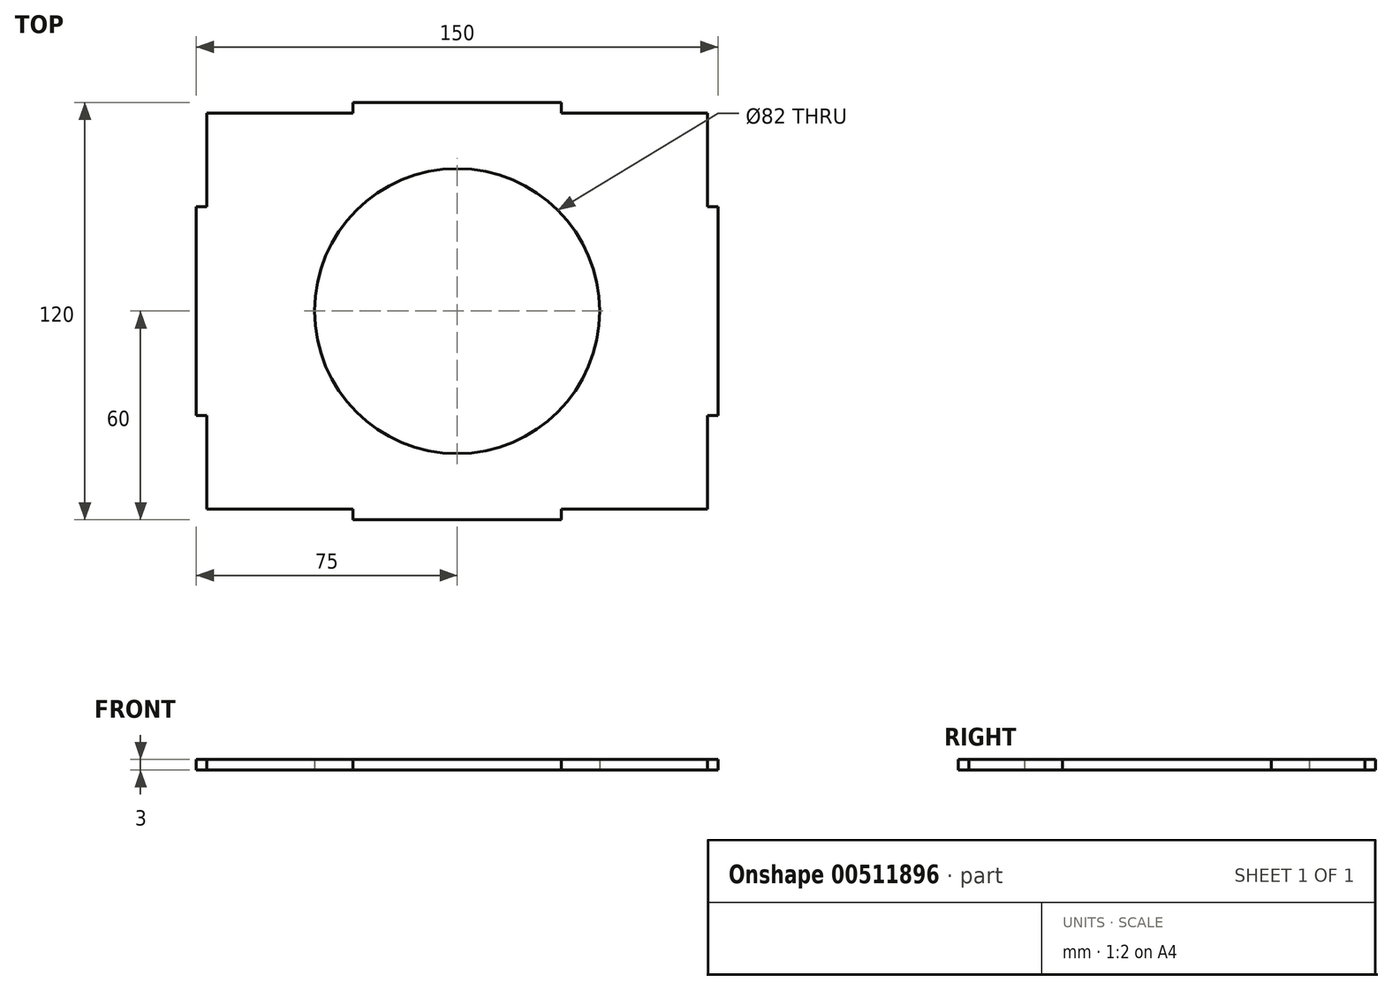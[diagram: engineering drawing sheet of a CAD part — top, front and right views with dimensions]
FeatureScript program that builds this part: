
annotation { "Feature Type Name" : "Feature", "Feature Type Description" : "" }
export const myFeature = defineFeature(function(context is Context, id is Id, definition is map)
    precondition{}
    {
        {
            var Q0;
            Q0=qCreatedBy(makeId("Top.planeOp"),FACE);
            var sketch = newSketch(context, id + "F0", { "sketchPlane" : qUnion([Q0])});
            skLineSegment(sketch, "E0.bottom", {"start": v(72, 57) * mm, "end": v(-72, 57) * mm});
            skLineSegment(sketch, "E0.top", {"start": v(72, -57) * mm, "end": v(-72, -57) * mm});
            skLineSegment(sketch, "E0.left", {"start": v(72, 57) * mm, "end": v(72, -57) * mm});
            skLineSegment(sketch, "E0.right", {"start": v(-72, 57) * mm, "end": v(-72, -57) * mm});
            skPoint(sketch, "E0.middle", {"position": v(0, 0) * mm});
            skCircle(sketch, "E1", {"center": v(0, 0) * mm, "radius": 41 * mm});
            skLineSegment(sketch, "E2.bottom", {"start": v(72, 30) * mm, "end": v(75, 30) * mm});
            skLineSegment(sketch, "E2.top", {"start": v(72, -30) * mm, "end": v(75, -30) * mm});
            skLineSegment(sketch, "E2.left", {"start": v(72, 30) * mm, "end": v(72, -30) * mm});
            skLineSegment(sketch, "E2.right", {"start": v(75, 30) * mm, "end": v(75, -30) * mm});
            skLineSegment(sketch, "E3.bottom", {"start": v(-72, -30) * mm, "end": v(-75, -30) * mm});
            skLineSegment(sketch, "E3.top", {"start": v(-72, 30) * mm, "end": v(-75, 30) * mm});
            skLineSegment(sketch, "E3.left", {"start": v(-72, -30) * mm, "end": v(-72, 30) * mm});
            skLineSegment(sketch, "E3.right", {"start": v(-75, -30) * mm, "end": v(-75, 30) * mm});
            skLineSegment(sketch, "E4.bottom", {"start": v(-30, 57) * mm, "end": v(30, 57) * mm});
            skLineSegment(sketch, "E4.top", {"start": v(-30, 60) * mm, "end": v(30, 60) * mm});
            skLineSegment(sketch, "E4.left", {"start": v(-30, 57) * mm, "end": v(-30, 60) * mm});
            skLineSegment(sketch, "E4.right", {"start": v(30, 57) * mm, "end": v(30, 60) * mm});
            skLineSegment(sketch, "E5.bottom", {"start": v(-30, -57) * mm, "end": v(30, -57) * mm});
            skLineSegment(sketch, "E5.top", {"start": v(-30, -60) * mm, "end": v(30, -60) * mm});
            skLineSegment(sketch, "E5.left", {"start": v(-30, -57) * mm, "end": v(-30, -60) * mm});
            skLineSegment(sketch, "E5.right", {"start": v(30, -57) * mm, "end": v(30, -60) * mm});
            skPoint(sketch, "E6", {"position": v(0, 57) * mm});
            skPoint(sketch, "E7", {"position": v(72, 0) * mm});
            skSolve(sketch);
        }
        {
            var Q0;
            Q0 = qSketchRegion(id + "F0", true);
            extrude(context, id + "F1", {"entities" : qUnion([Q0]), "depth" : 3 * mm, "offsetDistance" : 25 * mm});
        }
    });
